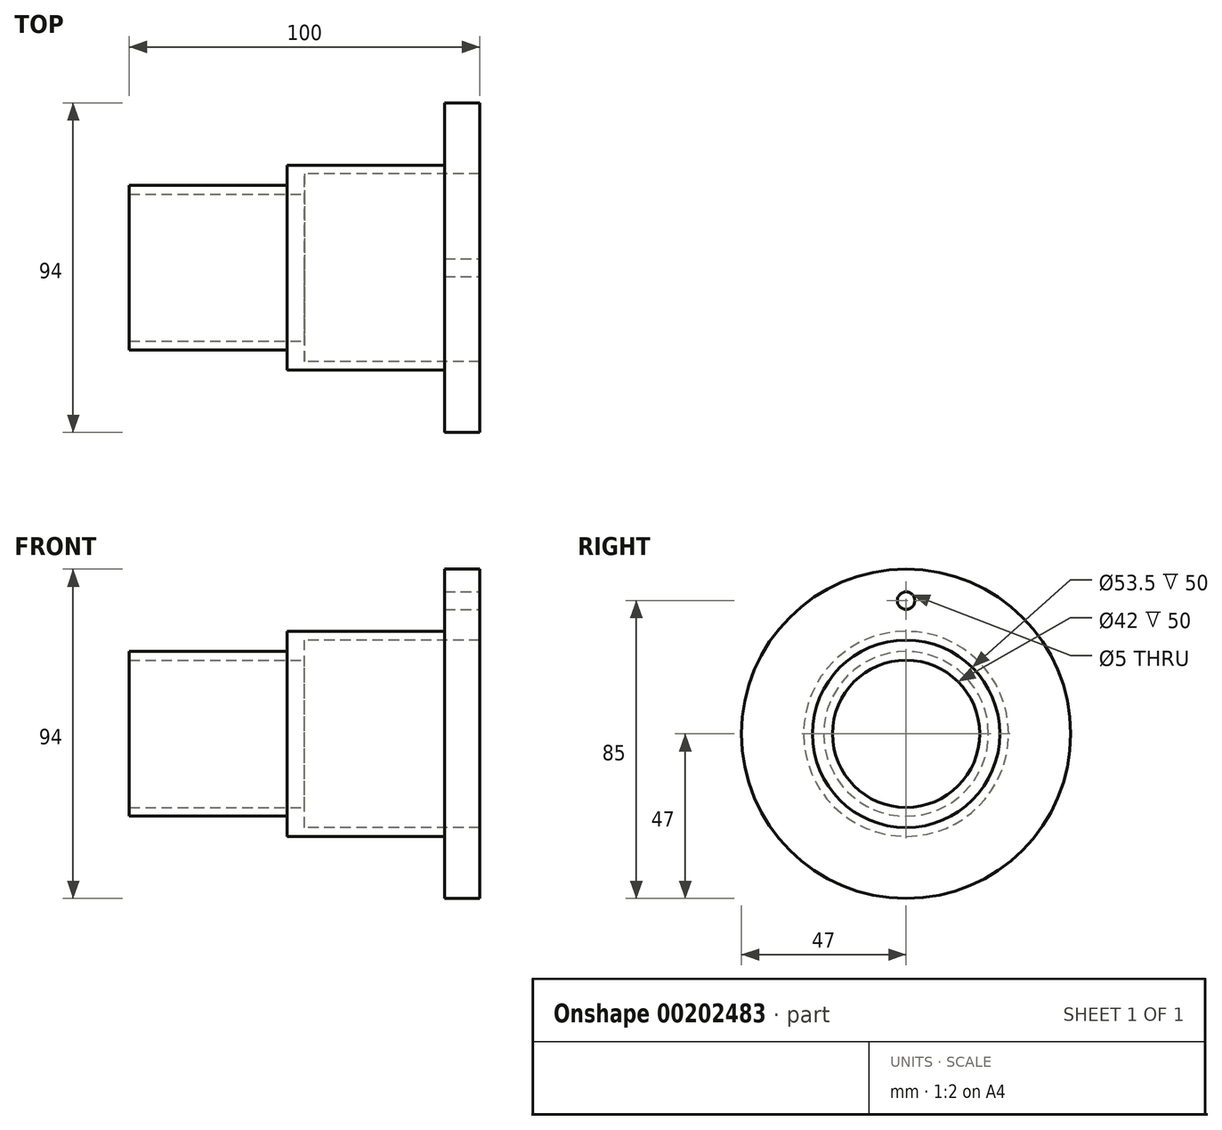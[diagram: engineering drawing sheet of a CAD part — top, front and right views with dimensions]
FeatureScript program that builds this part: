
annotation { "Feature Type Name" : "Feature", "Feature Type Description" : "" }
export const myFeature = defineFeature(function(context is Context, id is Id, definition is map)
    precondition{}
    {
        {
            var Q0;
            Q0=qCreatedBy(makeId("Right.planeOp"),FACE);
            var sketch = newSketch(context, id + "F0", { "sketchPlane" : qUnion([Q0])});
            skCircle(sketch, "E0", {"center": v(0, 0) * mm, "radius": 47 * mm});
            skCircle(sketch, "E1", {"center": v(0, 0) * mm, "radius": 26.75 * mm});
            skSolve(sketch);
        }
        {
            var Q0;
            Q0=makeQuery(id+"F0.imprint","IMPRINT",FACE,{"disambiguationData":[TD([[makeQuery(id+"F0.imprint","IMPRINT",EDGE,{"derivedFrom":sQuery(id+"F0.wireOp",EDGE,"E0")}),1.0]])]});
            extrude(context, id + "F1", {"entities" : qUnion([Q0]), "depth" : 10 * mm});
        }
        {
            var Q0;
            Q0=qCreatedBy(makeId("Front.planeOp"),FACE);
            var sketch = newSketch(context, id + "F2", { "sketchPlane" : qUnion([Q0])});
            skLineSegment(sketch, "E2", {"start": v(0, 29.25) * mm, "end": v(-45, 29.25) * mm});
            skLineSegment(sketch, "E3", {"start": v(-45, 29.25) * mm, "end": v(-45, 23.5) * mm});
            skLineSegment(sketch, "E4", {"start": v(-45, 23.5) * mm, "end": v(-90, 23.5) * mm});
            skLineSegment(sketch, "E5", {"start": v(-90, 23.5) * mm, "end": v(-90, 21) * mm});
            skLineSegment(sketch, "E6", {"start": v(0, 26.75) * mm, "end": v(0, 29.25) * mm});
            skLineSegment(sketch, "E7", {"start": v(0, 0) * mm, "end": v(-144.34, 0) * mm, "construction": true});
            skLineSegment(sketch, "E8", {"start": v(-90, 21) * mm, "end": v(-40, 21) * mm});
            skLineSegment(sketch, "E9", {"start": v(-40, 21) * mm, "end": v(-40, 26.75) * mm});
            skLineSegment(sketch, "E10", {"start": v(-40, 26.75) * mm, "end": v(0, 26.75) * mm});
            skSolve(sketch);
        }
        {
            var Q0;
            Q0=makeQuery(id+"F2.imprint","IMPRINT",FACE,{"disambiguationData":[TD([[makeQuery(id+"F2.imprint","IMPRINT",EDGE,{"derivedFrom":sQuery(id+"F2.wireOp",EDGE,"E2")}),1.0]])]});
            var Q1;
            Q1=sQuery(id+"F2.wireOp",EDGE,"E7");
            revolve(context, id + "F3", {"operationType" : NewBodyOperationType.ADD, "entities" : qUnion([Q0]), "axis" : qUnion([Q1]), "revolveType" : RevolveType.FULL});
        }
        {
            var Q0;
            Q0=makeQuery(id+"F1.opExtrude","CAP_FACE",FACE,{"disambiguationData":[OSD([sQuery(id+"F0.wireOp",EDGE,"E0"),sQuery(id+"F0.wireOp",EDGE,"E1")])],"isStart":false});
            var sketch = newSketch(context, id + "F4", { "sketchPlane" : qUnion([Q0])});
            skCircle(sketch, "E11", {"center": v(0, 0) * mm, "radius": 38 * mm, "construction": true});
            skCircle(sketch, "E12", {"center": v(0, 38) * mm, "radius": 2.5 * mm});
            skSolve(sketch);
        }
        {
            var Q0;
            Q0 = qSketchRegion(id + "F4", true);
            extrude(context, id + "F5", {"entities" : qUnion([Q0]), "operationType" : NewBodyOperationType.REMOVE, "endBound" : BoundingType.THROUGH_ALL, "oppositeDirection" : true, "depth" : 25 * mm});
        }
    });
